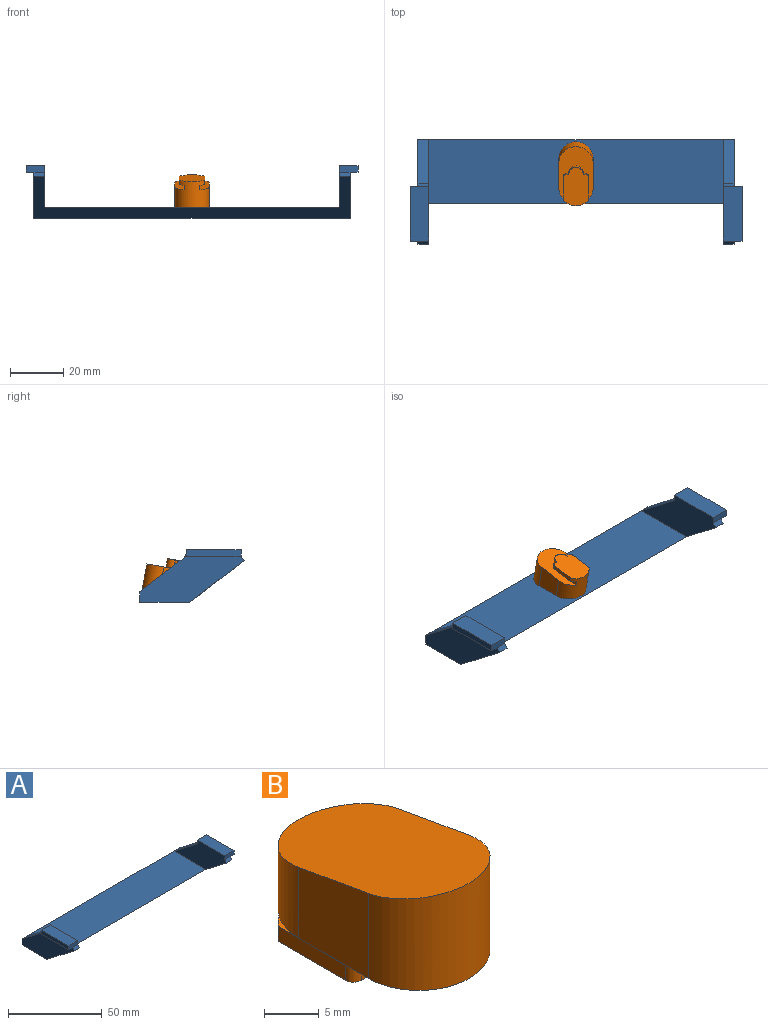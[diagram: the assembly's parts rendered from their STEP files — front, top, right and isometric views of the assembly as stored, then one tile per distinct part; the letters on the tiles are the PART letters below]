
ASSEMBLY  parts=2 mates=1
PART A: 24 faces, bbox 125x39.4x19.9 mm
  f0: plane 16.71x12.82mm, normal (0,0.61,0.79), area 84.2mm2, adj f4,f5,f11,f22
  f1: plane 4x1.59mm, normal (0,-0.79,0.61), area 8mm2, adj f4,f8,f11,f18
  f2: plane 16.71x12.82mm, normal (0,0.61,0.79), area 84.2mm2, adj f5,f6,f10,f23
  f3: plane 4x1.59mm, normal (0,-0.79,0.61), area 8mm2, adj f6,f8,f10,f14
  f4: plane 39.41x18.41mm, normal (-1,0,0), area 405.1mm2, adj f0,f1,f5,f7,f8,f17,f19,f22
  f5: plane 119x4mm, normal (0,1,0), area 476mm2, adj f0,f2,f4,f6,f7,f9
  f6: plane 39.41x18.41mm, normal (1,0,0), area 405.1mm2, adj f2,f3,f5,f7,f8,f12,f13,f23
  f7: plane 119x18.79mm, normal (0,0,-1), area 2235.7mm2, adj f4,f5,f6,f8
  f8: plane 119x20.63mm, normal (0,-0.61,-0.79), area 937.3mm2, adj f1,f3,f4,f6,f7,f9,f10,f11
  f9: plane 111x24mm, normal (0,0,1), area 2664mm2, adj f5,f8,f10,f11
  f10: plane 39.41x15.92mm, normal (-1,0,0), area 371.3mm2, adj f2,f3,f8,f9,f13,f14,f15,f23
  f11: plane 39.41x15.92mm, normal (1,0,0), area 371.3mm2, adj f0,f1,f8,f9,f18,f19,f20,f22
  f12: plane 20.71x3mm, normal (0,0,-1), area 62.1mm2, adj f6,f13,f14,f16
  f13: plane 7x2.5mm, normal (0,1,0), area 13.6mm2, adj f6,f10,f12,f15,f16,f23
  f14: plane 7x2.5mm, normal (0,-1,0), area 17.5mm2, adj f3,f10,f12,f15,f16
  f15: plane 20.71x7mm, normal (0,0,1), area 144.9mm2, adj f10,f13,f14,f16
  f16: plane 20.71x2.5mm, normal (1,0,0), area 51.8mm2, adj f12,f13,f14,f15
  f17: plane 20.71x3mm, normal (0,0,-1), area 62.1mm2, adj f4,f18,f19,f21
  f18: plane 7x2.5mm, normal (0,-1,0), area 17.5mm2, adj f1,f11,f17,f20,f21
  f19: plane 7x2.5mm, normal (0,1,0), area 13.6mm2, adj f4,f11,f17,f20,f21,f22
  f20: plane 20.71x7mm, normal (0,0,1), area 144.9mm2, adj f11,f18,f19,f21
  f21: plane 20.71x2.5mm, normal (-1,0,0), area 51.8mm2, adj f17,f18,f19,f20
  f22: cylinder r=2mm len=4mm, axis (-1,0,0), area 7.3mm2, adj f0,f4,f11,f19
  f23: cylinder r=2mm len=4mm, axis (1,0,0), area 7.3mm2, adj f2,f6,f10,f13
PART B: 18 faces, bbox 13x22x14 mm
  f0: cylinder r=6.5mm len=13mm, axis (0,0,-1), area 175.5mm2, adj f2,f5,f6,f7,f11,f12,f13,f14
  f1: cylinder r=6.5mm len=13mm, axis (0,0,-1), area 209mm2, adj f2,f5,f12,f17
  f2: plane 9.5x9mm, normal (1,0,0), area 78.4mm2, adj f0,f1,f12,f17
  f3: plane 3.35x1.06mm, normal (0,-1,0), area 2.1mm2, adj f4,f6,f10,f12,f13,f14
  f4: cylinder r=1mm len=1.67mm, axis (0,0,-1), area 2.6mm2, adj f3,f6,f11,f13
  f5: plane 9.5x9mm, normal (-1,0,0), area 78.4mm2, adj f0,f1,f12,f17
  f6: plane 14.66x9.68mm, normal (0,0,-1), area 120.3mm2, adj f0,f3,f4,f7,f8,f9,f10,f11
  f7: plane 8.72x1.67mm, normal (-1,0,0), area 14.6mm2, adj f0,f6,f8,f15
  f8: cylinder r=1mm len=1.67mm, axis (0,0,-1), area 2.6mm2, adj f6,f7,f9,f15
  f9: plane 3.35x1.06mm, normal (0,-1,0), area 2.1mm2, adj f6,f8,f10,f12,f15,f16
  f10: cylinder r=2.78mm len=5.56mm, axis (0,0,-1), area 29.3mm2, adj f3,f6,f9,f12
  f11: plane 8.72x1.67mm, normal (1,0,0), area 14.6mm2, adj f0,f4,f6,f13
  f12: plane 21.27x13mm, normal (0,0,-1), area 167.7mm2, adj f0,f1,f2,f3,f5,f9,f10,f14
  f13: plane 11.15x1.84mm, normal (0,0,1), area 19.1mm2, adj f0,f3,f4,f11,f14
  f14: plane 11.15x1.68mm, normal (1,0,0), area 18.7mm2, adj f0,f3,f12,f13
  f15: plane 11.15x1.84mm, normal (0,0,1), area 19.1mm2, adj f0,f7,f8,f9,f16
  f16: plane 11.15x1.68mm, normal (-1,0,0), area 18.7mm2, adj f0,f9,f12,f15
  f17: plane 22x13mm, normal (0,0.17,0.98), area 253.6mm2, adj f0,f1,f2,f5
PLACE A t=(22.19,93.24,-10.56)mm
PLACE B rot(axis=(-1,0,0),170deg) t=(81.69,79.14,5.32)mm
MATE planar B.f17 <-> A.f9  axis (0,0,-1) through (81.69,81.24,-6.56)mm
